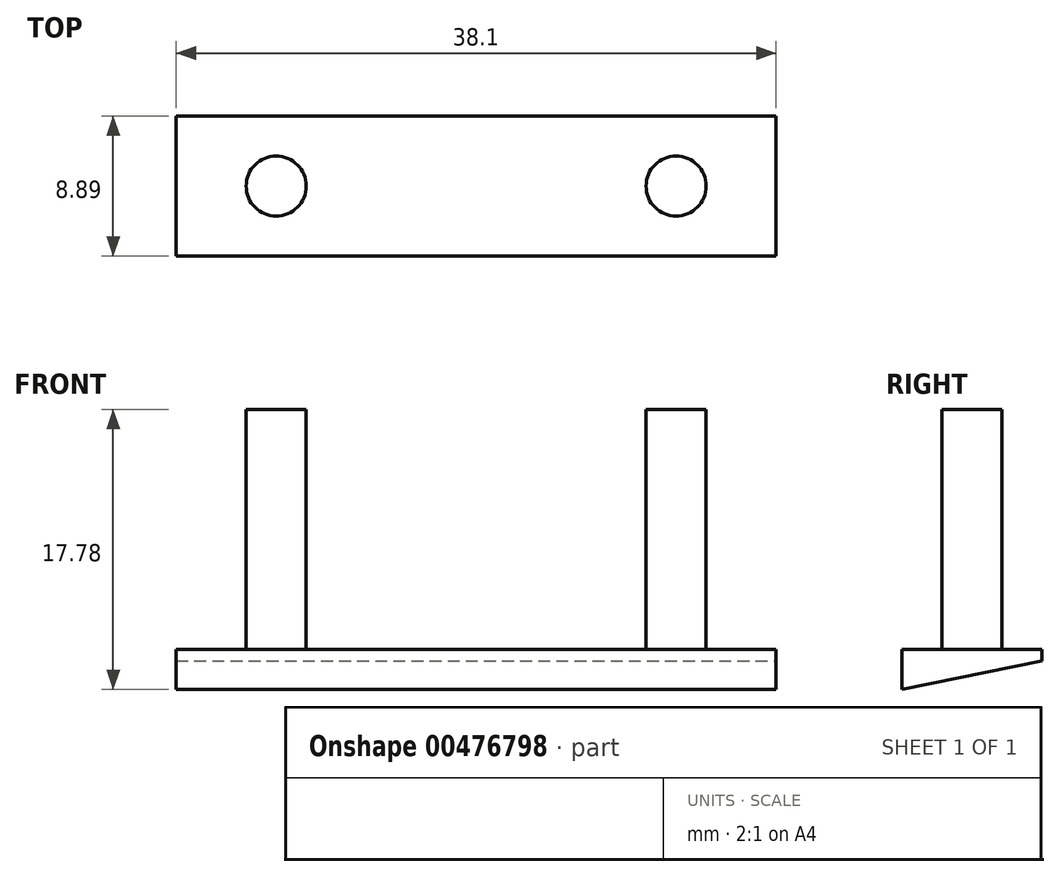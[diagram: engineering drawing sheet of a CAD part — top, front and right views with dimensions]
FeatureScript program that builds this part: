
annotation { "Feature Type Name" : "Feature", "Feature Type Description" : "" }
export const myFeature = defineFeature(function(context is Context, id is Id, definition is map)
    precondition{}
    {
        {
            var Q0;
            Q0=qCreatedBy(makeId("Top.planeOp"),FACE);
            var sketch = newSketch(context, id + "F0", { "sketchPlane" : qUnion([Q0])});
            skLineSegment(sketch, "E0.bottom", {"start": v(0, 0) * mm, "end": v(38.1, 0) * mm});
            skLineSegment(sketch, "E0.top", {"start": v(0, 8.9) * mm, "end": v(38.1, 8.9) * mm});
            skLineSegment(sketch, "E0.left", {"start": v(0, 0) * mm, "end": v(0, 8.9) * mm});
            skLineSegment(sketch, "E0.right", {"start": v(38.1, 0) * mm, "end": v(38.1, 8.9) * mm});
            skSolve(sketch);
        }
        {
            var Q0;
            Q0 = qSketchRegion(id + "F0", true);
            extrude(context, id + "F1", {"entities" : qUnion([Q0]), "depth" : 2.54 * mm});
        }
        {
            var Q0;
            Q0=makeQuery(id+"F1.opExtrude","CAP_FACE",FACE,{"disambiguationData":[OSD([sQuery(id+"F0.wireOp",EDGE,"E0.bottom"),sQuery(id+"F0.wireOp",EDGE,"E0.top"),sQuery(id+"F0.wireOp",EDGE,"E0.left"),sQuery(id+"F0.wireOp",EDGE,"E0.right")])],"isStart":false});
            var sketch = newSketch(context, id + "F2", { "sketchPlane" : qUnion([Q0])});
            skCircle(sketch, "E1", {"center": v(6.35, 4.45) * mm, "radius": 1.9 * mm});
            skCircle(sketch, "E2", {"center": v(31.75, 4.45) * mm, "radius": 1.9 * mm});
            skSolve(sketch);
        }
        {
            var Q0;
            Q0 = qSketchRegion(id + "F2", true);
            extrude(context, id + "F3", {"entities" : qUnion([Q0]), "operationType" : NewBodyOperationType.ADD, "depth" : 15.24 * mm});
        }
        {
            var Q0;
            Q0=makeQuery(id+"F1.opExtrude","SWEPT_FACE",FACE,{"disambiguationData":[OSD([sQuery(id+"F0.wireOp",EDGE,"E0.right")])]});
            var sketch = newSketch(context, id + "F4", { "sketchPlane" : qUnion([Q0])});
            skLineSegment(sketch, "E3", {"start": v(8.89, 1.8) * mm, "end": v(0, 0) * mm});
            skLineSegment(sketch, "E4", {"start": v(0, 0) * mm, "end": v(8.9, 0) * mm});
            skLineSegment(sketch, "E5", {"start": v(8.89, 0) * mm, "end": v(8.89, 1.8) * mm});
            skSolve(sketch);
        }
        {
            var Q0;
            Q0 = qSketchRegion(id + "F4", true);
            extrude(context, id + "F5", {"entities" : qUnion([Q0]), "operationType" : NewBodyOperationType.REMOVE, "oppositeDirection" : true, "depth" : 38.1 * mm});
        }
    });
